FCSTD DOCUMENT  (FreeCAD 0.16R)
Label: bitholder2
License: All rights reserved
LicenseURL: http://en.wikipedia.org/wiki/All_rights_reserved
objects: Sketcher::SketchObject×8, PartDesign::Pocket×6, PartDesign::Pad×2, PartDesign::LinearPattern×2, PartDesign::Chamfer×1, Mesh::Feature×1
note: 27 computed .brp shape members not serialized (recipe doc carries the construction recipe); baked Part::Feature solids carry a one-line shape summary decoded from their .brp

FEATURE [Sketcher::SketchObject] Sketch
  sketch-geometry (4):
    g0: LineSegment StartX=-65 StartY=35 StartZ=0 EndX=65 EndY=35 EndZ=0
    g1: LineSegment StartX=65 StartY=35 StartZ=0 EndX=65 EndY=-35 EndZ=0
    g2: LineSegment StartX=65 StartY=-35 StartZ=0 EndX=-65 EndY=-35 EndZ=0
    g3: LineSegment StartX=-65 StartY=-35 StartZ=0 EndX=-65 EndY=35 EndZ=0
  constraints (11):
    c: Coincident(g0,g1)
    c: Coincident(g1,g2)
    c: Coincident(g2,g3)
    c: Coincident(g3,g0)
    c: Horizontal(g0)
    c: Horizontal(g2)
    c: Vertical(g1)
    c: Vertical(g3)
    c: Symmetric(g1,g0,g-1)
    c: Distance(g3) = 70
    c: Distance(g0) = 130
FEATURE [PartDesign::Pad] Pad
  Length = 20
  Length2 = 100
  Sketch = -> Sketch
  Type = 0
FEATURE [Sketcher::SketchObject] Sketch001
  ExternalGeometry = -> [Pad]
  Placement = pos=(0,0,20) rot=(0,0,1;0rad)
  Support = -> Pad [Face6]
  sketch-geometry (6):
    g0: Circle CenterX=-40 CenterY=25 CenterZ=0 NormalX=0 NormalY=0 NormalZ=1 Radius=2.2
    g1: Circle CenterX=-10 CenterY=25 CenterZ=0 NormalX=0 NormalY=0 NormalZ=1 Radius=3.3
    g2: Circle CenterX=-30 CenterY=25 CenterZ=0 NormalX=0 NormalY=0 NormalZ=1 Radius=2.2
    g3: Circle CenterX=-20 CenterY=25 CenterZ=0 NormalX=0 NormalY=0 NormalZ=1 Radius=2.7
    g4: LineSegment [constr] StartX=-120 StartY=25 StartZ=0 EndX=80 EndY=25 EndZ=0
    g5: Circle CenterX=-50 CenterY=25 CenterZ=0 NormalX=0 NormalY=0 NormalZ=1 Radius=1.8
  constraints (19):
    c: Radius(g0) = 2.2
    c: Radius(g2) = 2.2
    c: Radius(g1) = 3.3
    c: Radius(g3) = 2.7
    c: Horizontal(g4)
    c: PointOnObject(g0,g4)
    c: PointOnObject(g2,g4)
    c: PointOnObject(g3,g4)
    c: PointOnObject(g1,g4)
    c: DistanceY(g4) = 25
    c: Distance(g2,g0) = 10
    c: Distance(g3,g2) = 10
    c: Distance(g3,g1) = 10
    c: Distance(g4) = 200
    c: DistanceX(g4) = 80
    c: PointOnObject(g5,g4)
    c: Distance(g5,g0) = 10
    c: Distance(g5,g-3) = 15
    c: Radius(g5) = 1.8
FEATURE [PartDesign::Pocket] Pocket
  Length = 19
  Sketch = -> Sketch001
  Type = 0
FEATURE [PartDesign::LinearPattern] LinearPattern
  Direction = -> Sketch001 [V_Axis]
  Length = 40
  Occurrences = 5
  Originals = -> [Pocket]
  Reversed = true
FEATURE [Sketcher::SketchObject] Sketch002
  Placement = pos=(0,0,20) rot=(0,0,1;0rad)
  Support = -> LinearPattern [Face5]
  sketch-geometry (3):
    g0: Circle CenterX=8 CenterY=-20 CenterZ=0 NormalX=0 NormalY=0 NormalZ=1 Radius=5.5
    g1: Circle CenterX=28 CenterY=-20 CenterZ=0 NormalX=0 NormalY=0 NormalZ=1 Radius=7
    g2: Circle CenterX=48 CenterY=-20 CenterZ=0 NormalX=0 NormalY=0 NormalZ=1 Radius=8
  constraints (9):
    c: Radius(g2) = 8
    c: Radius(g1) = 7
    c: Radius(g0) = 5.5
    c: Distance(g2,g1) = 20
    c: Distance(g0,g1) = 20
    c: DistanceY(g0) = -20
    c: DistanceY(g1) = -20
    c: DistanceY(g2) = -20
    c: DistanceX(g0) = 8
FEATURE [PartDesign::Pocket] Pocket001
  Length = 19
  Sketch = -> Sketch002
  Type = 0
FEATURE [PartDesign::LinearPattern] LinearPattern001
  Direction = -> Sketch002 [V_Axis]
  Length = 35
  Occurrences = 3
  Originals = -> [Pocket001]
FEATURE [Sketcher::SketchObject] Sketch007
  ExternalGeometry = -> [LinearPattern001]
  Placement = pos=(65,0,0) rot=(0.57735,0.57735,0.57735;2.0944rad)
  Support = -> LinearPattern001 [Face3]
  sketch-geometry (3):
    g0: LineSegment StartX=35 StartY=20 StartZ=0 EndX=55 EndY=20 EndZ=0
    g1: LineSegment StartX=55 StartY=20 StartZ=0 EndX=35 EndY=0 EndZ=0
    g2: LineSegment StartX=35 StartY=0 StartZ=0 EndX=35 EndY=20 EndZ=0
  constraints (7):
    c: Coincident(g-4,g0)
    c: Horizontal(g0)
    c: Coincident(g0,g1)
    c: Coincident(g1,g-5)
    c: Coincident(g1,g2)
    c: Coincident(g2,g0)
    c: Distance(g0) = 20
FEATURE [PartDesign::Pad] Pad001
  Length = 15
  Length2 = 145
  Sketch = -> Sketch007
  Type = 4
FEATURE [Sketcher::SketchObject] Sketch008
  ExternalGeometry = -> [Pad001]
  Placement = pos=(0,17.5,-17.5) rot=(0,0.92388,0.382683;3.14159rad)
  Support = -> Pad001 [Face3]
  sketch-geometry (2):
    g0: Circle CenterX=-72.5 CenterY=38.8909 CenterZ=0 NormalX=0 NormalY=0 NormalZ=1 Radius=3
    g1: Circle CenterX=72.5 CenterY=38.8909 CenterZ=0 NormalX=0 NormalY=0 NormalZ=1 Radius=3
  constraints (4):
    c: Symmetric(g-5,g-6,g1)
    c: Symmetric(g-7,g-5,g0)
    c: Radius(g0) = 3
    c: Equal(g0,g1)
FEATURE [PartDesign::Pocket] Pocket002
  Length = 5
  Sketch = -> Sketch008
  Type = 1
FEATURE [Sketcher::SketchObject] Sketch009
  ExternalGeometry = -> [Pocket002]
  Placement = pos=(0,0,20) rot=(0,0,1;0rad)
  Support = -> Pocket002 [Face8]
  sketch-geometry (10):
    g0: Circle CenterX=-50 CenterY=-25 CenterZ=0 NormalX=0 NormalY=0 NormalZ=1 Radius=4
    g1: Circle CenterX=-40 CenterY=-25 CenterZ=0 NormalX=0 NormalY=0 NormalZ=1 Radius=4
    g2: Circle CenterX=-30 CenterY=-25 CenterZ=0 NormalX=0 NormalY=0 NormalZ=1 Radius=4
    g3: Circle CenterX=-20 CenterY=-25 CenterZ=0 NormalX=0 NormalY=0 NormalZ=1 Radius=4
    g4: Circle CenterX=-10 CenterY=-25 CenterZ=0 NormalX=0 NormalY=0 NormalZ=1 Radius=4
    g5: Circle CenterX=49.7579 CenterY=29.1321 CenterZ=0 NormalX=0 NormalY=0 NormalZ=1 Radius=2
    g6: Circle CenterX=58.0142 CenterY=28.8928 CenterZ=0 NormalX=0 NormalY=0 NormalZ=1 Radius=2.5
    g7: LineSegment [constr] StartX=-59.9314 StartY=-25 StartZ=0 EndX=4.92298 EndY=-25 EndZ=0
    g8: Circle CenterX=16.5976 CenterY=27.3513 CenterZ=0 NormalX=0 NormalY=0 NormalZ=1 Radius=5
    g9: Circle CenterX=37.0742 CenterY=27.6962 CenterZ=0 NormalX=0 NormalY=0 NormalZ=1 Radius=5
  constraints (21):
    c: Radius(g5) = 2
    c: Radius(g6) = 2.5
    c: Radius(g0) = 4
    c: Radius(g3) = 4
    c: Equal(g3,g4)
    c: Equal(g3,g2)
    c: Equal(g3,g1)
    c: Horizontal(g7)
    c: PointOnObject(g0,g7)
    c: PointOnObject(g1,g7)
    c: PointOnObject(g2,g7)
    c: PointOnObject(g3,g7)
    c: PointOnObject(g4,g7)
    c: DistanceY(g7) = -25
    c: Distance(g0,g1) = 10
    c: Distance(g1,g2) = 10
    c: Distance(g2,g3) = 10
    c: Distance(g4,g3) = 10
    c: Radius(g9) = 5
    c: Equal(g9,g8)
    c: Distance(g0,g-3) = 15
FEATURE [PartDesign::Pocket] Pocket003
  Length = 19
  Sketch = -> Sketch009
  Type = 0
FEATURE [Sketcher::SketchObject] Sketch010
  ExternalGeometry = -> [Pocket003]
  Placement = pos=(-80,0,0) rot=(0.57735,-0.57735,-0.57735;2.0944rad)
  Support = -> Pocket003 [Face1]
  sketch-geometry (3):
    g0: LineSegment StartX=-43.264 StartY=22.4061 StartZ=0 EndX=-33.0195 EndY=12.1617 EndZ=0
    g1: LineSegment StartX=-33.0195 StartY=12.1617 StartZ=0 EndX=-31.8208 EndY=25.1005 EndZ=0
    g2: LineSegment StartX=-31.8208 StartY=25.1005 StartZ=0 EndX=-43.264 EndY=22.4061 EndZ=0
  constraints (5):
    c: Coincident(g0,g1)
    c: Coincident(g1,g2)
    c: Coincident(g2,g0)
    c: Parallel(g0,g-3)
    c: Distance(g0,g-3) = 10
FEATURE [PartDesign::Pocket] Pocket004
  Length = 15
  Sketch = -> Sketch010
  Type = 0
FEATURE [Sketcher::SketchObject] Sketch011
  ExternalGeometry = -> [Pocket004]
  Placement = pos=(80,0,0) rot=(0.57735,0.57735,0.57735;2.0944rad)
  Support = -> Pocket004 [Face9]
  sketch-geometry (3):
    g0: LineSegment StartX=45.3287 StartY=24.4708 StartZ=0 EndX=28.0463 EndY=7.1884 EndZ=0
    g1: LineSegment StartX=28.0463 StartY=7.1884 StartZ=0 EndX=25.5227 EndY=31.359 EndZ=0
    g2: LineSegment StartX=25.5227 StartY=31.359 StartZ=0 EndX=45.3287 EndY=24.4708 EndZ=0
  constraints (5):
    c: Coincident(g0,g1)
    c: Coincident(g1,g2)
    c: Coincident(g2,g0)
    c: Parallel(g0,g-3)
    c: Distance(g0,g-3) = 10
FEATURE [PartDesign::Pocket] Pocket005
  Length = 15
  Sketch = -> Sketch011
  Type = 0
FEATURE [PartDesign::Chamfer] Chamfer
  Base = -> Pocket005 [Edge81,Edge84,Edge67,Edge66,Edge68,Edge69,Edge55,Edge54,Edge53,Edge83,Edge65,Edge82,Edge64,Edge58,Edge59,Edge57,Edge52,Edge51,Edge50,Edge62,Edge80,Edge63,Edge48,Edge46,Edge43,Edge44,Edge45,Edge49,Edge61,Edge79,Edge77,Edge75,Edge85,Edge74,Edge76,Edge78,Edge56,Edge60,Edge71,Edge73,+9 more]
  Size = 0.7
FEATURE [Mesh::Feature] Mesh  label="Chamfer (Meshed)"
